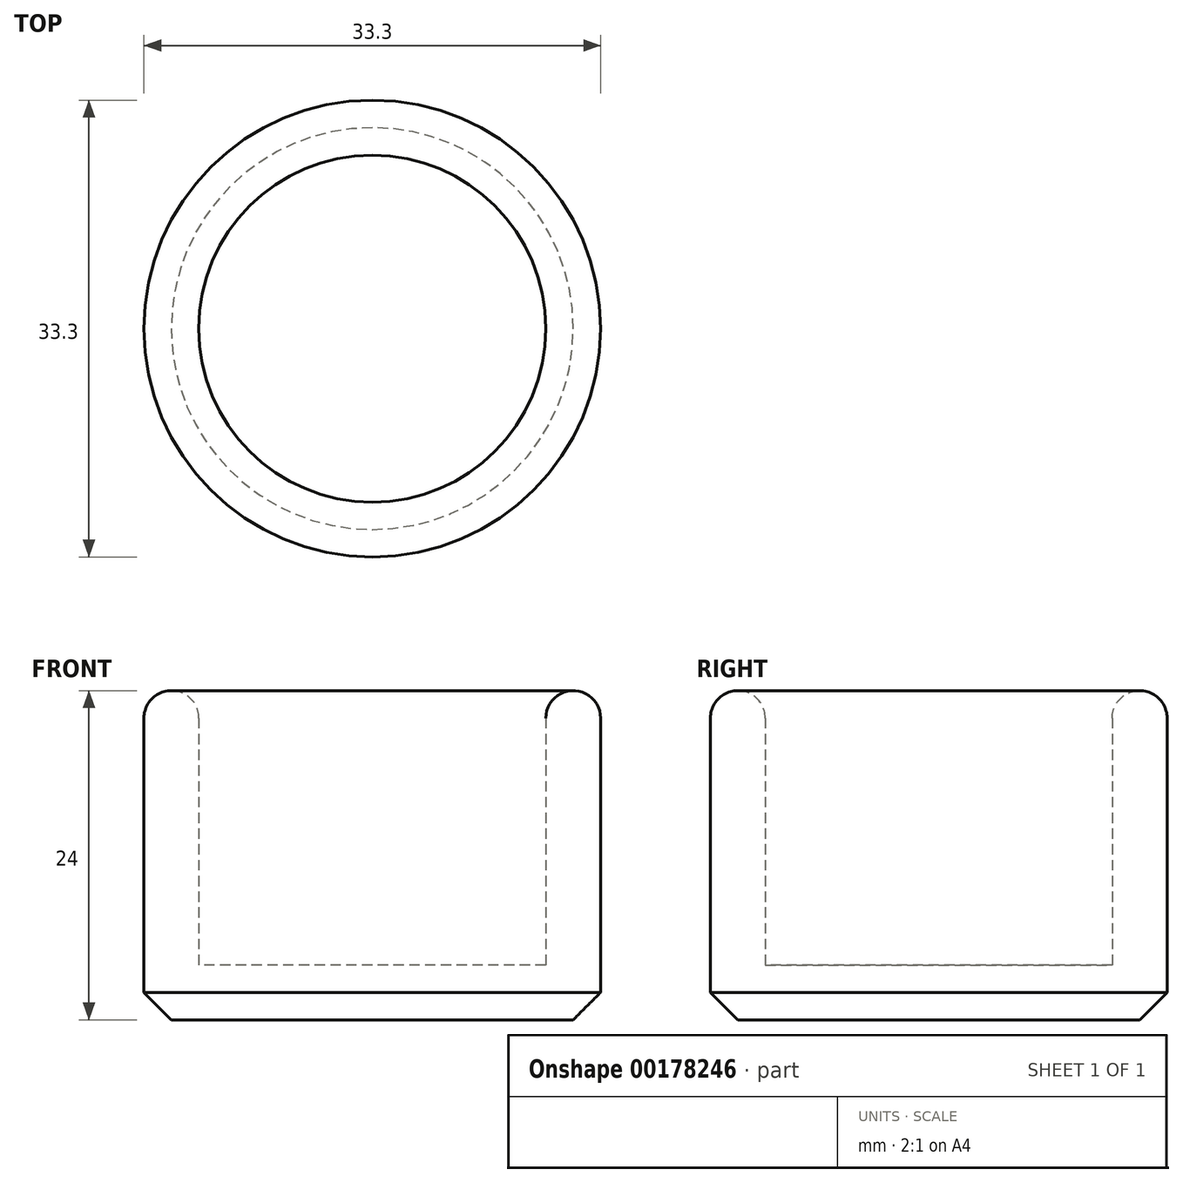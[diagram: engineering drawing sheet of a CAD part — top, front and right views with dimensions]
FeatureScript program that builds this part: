
annotation { "Feature Type Name" : "Feature", "Feature Type Description" : "" }
export const myFeature = defineFeature(function(context is Context, id is Id, definition is map)
    precondition{}
    {
        {
            var Q0;
            Q0=qCreatedBy(makeId("Top.planeOp"),FACE);
            var sketch = newSketch(context, id + "F0", { "sketchPlane" : qUnion([Q0])});
            skCircle(sketch, "E0", {"center": v(0, 0) * mm, "radius": 12.65 * mm});
            skCircle(sketch, "E1.0", {"center": v(0, 0) * mm, "radius": 16.65 * mm});
            skSolve(sketch);
        }
        {
            var Q0;
            Q0=makeQuery(id+"F0.imprint","IMPRINT",FACE,{"disambiguationData":[TD([[makeQuery(id+"F0.imprint","IMPRINT",EDGE,{"derivedFrom":sQuery(id+"F0.wireOp",EDGE,"E0")}),-1.0]])]});
            extrude(context, id + "F1", {"entities" : qUnion([Q0]), "depth" : 20 * mm});
        }
        {
            var Q0;
            Q0=makeQuery(id+"F0.imprint","IMPRINT",FACE,{"disambiguationData":[TD([[makeQuery(id+"F0.imprint","IMPRINT",EDGE,{"derivedFrom":sQuery(id+"F0.wireOp",EDGE,"E0")}),-1.0]])]});
            var Q1;
            Q1=makeQuery(id+"F0.imprint","IMPRINT",FACE,{"disambiguationData":[TD([[makeQuery(id+"F0.imprint","IMPRINT",EDGE,{"derivedFrom":sQuery(id+"F0.wireOp",EDGE,"E0")}),1.0]])]});
            extrude(context, id + "F2", {"entities" : qUnion([Q0, Q1]), "operationType" : NewBodyOperationType.ADD, "oppositeDirection" : true, "depth" : 4 * mm});
        }
        {
            var Q0;
            Q0=makeQuery(id+"F2.opExtrude","CAP_EDGE",EDGE,{"disambiguationData":[OSD([sQuery(id+"F0.wireOp",EDGE,"E1.0")])],"isStart":false});
            chamfer(context, id + "F3", {"entities" : qUnion([Q0]), "width" : 2 * mm, "tangentPropagation" : true});
        }
        {
            var Q0;
            Q0=makeQuery(id+"F1.opExtrude","CAP_EDGE",EDGE,{"disambiguationData":[OSD([sQuery(id+"F0.wireOp",EDGE,"E0")])],"isStart":false});
            var Q1;
            Q1=makeQuery(id+"F1.opExtrude","CAP_EDGE",EDGE,{"disambiguationData":[OSD([sQuery(id+"F0.wireOp",EDGE,"E1.0")])],"isStart":false});
            fillet(context, id + "F4", {"entities" : qUnion([Q0, Q1]), "radius" : 2 * mm, "tangentPropagation" : true, "allowEdgeOverflow" : false});
        }
    });
